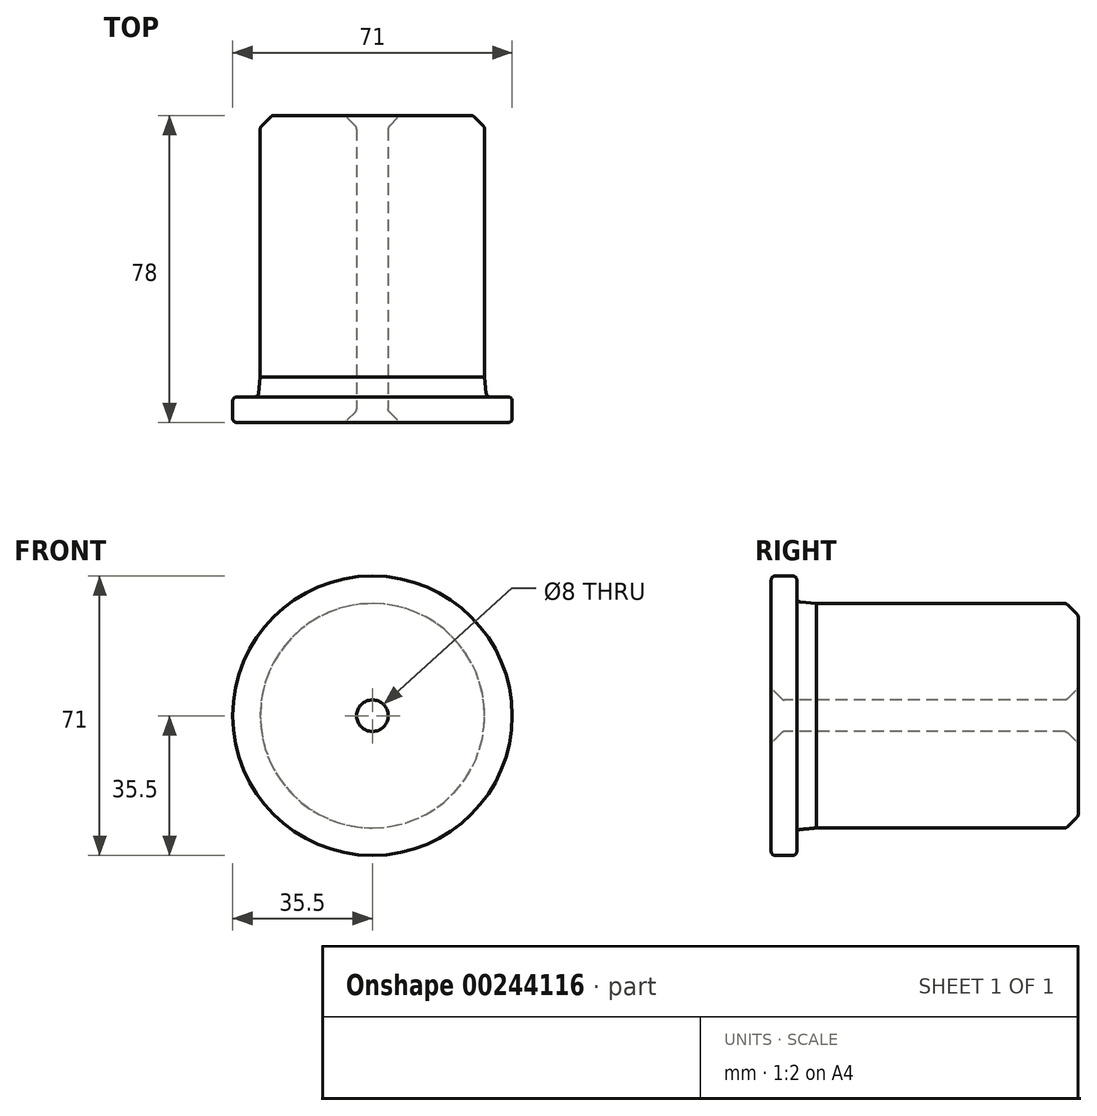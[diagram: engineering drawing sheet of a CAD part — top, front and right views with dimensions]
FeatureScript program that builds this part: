
annotation { "Feature Type Name" : "Feature", "Feature Type Description" : "" }
export const myFeature = defineFeature(function(context is Context, id is Id, definition is map)
    precondition{}
    {
        {
            var Q0;
            Q0=qCreatedBy(makeId("Right.planeOp"),FACE);
            var sketch = newSketch(context, id + "F0", { "sketchPlane" : qUnion([Q0])});
            skLineSegment(sketch, "E0", {"start": v(-14.96, 0) * mm, "end": v(91.12, 0) * mm, "construction": true});
            skLineSegment(sketch, "E1.bottom", {"start": v(0, 4) * mm, "end": v(6.5, 4) * mm});
            skLineSegment(sketch, "E1.top", {"start": v(0, 35.5) * mm, "end": v(6.5, 35.5) * mm});
            skLineSegment(sketch, "E1.left", {"start": v(0, 4) * mm, "end": v(0, 35.5) * mm});
            skLineSegment(sketch, "E1.right", {"start": v(6.5, 4) * mm, "end": v(6.5, 35.5) * mm});
            skLineSegment(sketch, "E2.bottom", {"start": v(78, 4) * mm, "end": v(6.5, 4) * mm});
            skLineSegment(sketch, "E2.top", {"start": v(78, 28.5) * mm, "end": v(6.5, 28.5) * mm});
            skLineSegment(sketch, "E2.left", {"start": v(78, 4) * mm, "end": v(78, 28.5) * mm});
            skLineSegment(sketch, "E2.right", {"start": v(6.5, 4) * mm, "end": v(6.5, 28.5) * mm});
            skSolve(sketch);
        }
        {
            var Q0;
            Q0=makeQuery(id+"F0.imprint","IMPRINT",FACE,{"disambiguationData":[TD([[makeQuery(id+"F0.imprint","IMPRINT",EDGE,{"derivedFrom":sQuery(id+"F0.wireOp",EDGE,"E1.bottom")}),1.0]])]});
            var Q1;
            Q1=makeQuery(id+"F0.imprint","IMPRINT",FACE,{"disambiguationData":[TD([[makeQuery(id+"F0.imprint","IMPRINT",EDGE,{"derivedFrom":sQuery(id+"F0.wireOp",EDGE,"E2.bottom")}),-1.0]])]});
            var Q2;
            Q2=sQuery(id+"F0.wireOp",EDGE,"E0");
            revolve(context, id + "F1", {"entities" : qUnion([Q0, Q1]), "axis" : qUnion([Q2]), "revolveType" : RevolveType.FULL});
        }
        {
            var Q0;
            Q0=makeQuery(id+"F1.opRevolve","SWEPT_EDGE",EDGE,{"disambiguationData":[OSD([sQuery(id+"F0.wireOp",EDGE,"E2.top"),sQuery(id+"F0.wireOp",EDGE,"E2.left")])]});
            var Q1;
            Q1=makeQuery(id+"F1.opRevolve","SWEPT_EDGE",EDGE,{"disambiguationData":[OSD([sQuery(id+"F0.wireOp",EDGE,"E2.bottom"),sQuery(id+"F0.wireOp",EDGE,"E2.left")])]});
            var Q2;
            Q2=makeQuery(id+"F1.opRevolve","SWEPT_EDGE",EDGE,{"disambiguationData":[OSD([sQuery(id+"F0.wireOp",EDGE,"E1.bottom"),sQuery(id+"F0.wireOp",EDGE,"E1.left")])]});
            chamfer(context, id + "F2", {"entities" : qUnion([Q0, Q1, Q2]), "width" : 3 * mm, "tangentPropagation" : true});
        }
        {
            var Q0;
            Q0=makeQuery(id+"F1.opRevolve","SWEPT_EDGE",EDGE,{"disambiguationData":[OSD([sQuery(id+"F0.wireOp",EDGE,"E1.right"),sQuery(id+"F0.wireOp",EDGE,"E2.top"),sQuery(id+"F0.wireOp",EDGE,"E2.right")])]});
            chamfer(context, id + "F3", {"entities" : qUnion([Q0]), "chamferType" : ChamferType.TWO_OFFSETS, "width1" : 5 * mm, "oppositeDirection" : true, "width2" : 0.5 * mm, "tangentPropagation" : true});
        }
        {
            var Q0;
            Q0=makeQuery(id+"F1.opRevolve","SWEPT_EDGE",EDGE,{"disambiguationData":[OSD([sQuery(id+"F0.wireOp",EDGE,"E1.top"),sQuery(id+"F0.wireOp",EDGE,"E1.left")])]});
            var Q1;
            Q1=makeQuery(id+"F1.opRevolve","SWEPT_EDGE",EDGE,{"disambiguationData":[OSD([sQuery(id+"F0.wireOp",EDGE,"E1.top"),sQuery(id+"F0.wireOp",EDGE,"E1.right")])]});
            var Q2;
            {var subQ0=sQuery(id+"F0.wireOp",EDGE,"E1.right");Q2=makeQuery(id+"F3.opChamfer","BLEND_EDGE",EDGE,{"blendedFrom":[makeQuery(id+"F1.opRevolve","SWEPT_EDGE",EDGE,{"disambiguationData":[OSD([subQ0,sQuery(id+"F0.wireOp",EDGE,"E2.top"),sQuery(id+"F0.wireOp",EDGE,"E2.right")])]}),makeQuery(id+"F1.opRevolve","SWEPT_FACE",FACE,{"disambiguationData":[OSD([subQ0])]})],"blendedInto":[makeQuery(id+"F1.opRevolve","SWEPT_FACE",FACE,{"disambiguationData":[OSD([subQ0])]})]});}
            var Q3;
            {var subQ0=sQuery(id+"F0.wireOp",EDGE,"E2.top");Q3=makeQuery(id+"F2.opChamfer","BLEND_EDGE",EDGE,{"blendedFrom":[makeQuery(id+"F1.opRevolve","SWEPT_EDGE",EDGE,{"disambiguationData":[OSD([subQ0,sQuery(id+"F0.wireOp",EDGE,"E2.left")])]}),makeQuery(id+"F1.opRevolve","SWEPT_FACE",FACE,{"disambiguationData":[OSD([subQ0])]})],"blendedInto":[makeQuery(id+"F1.opRevolve","SWEPT_FACE",FACE,{"disambiguationData":[OSD([subQ0])]})]});}
            var Q4;
            {var subQ0=sQuery(id+"F0.wireOp",EDGE,"E2.left");Q4=makeQuery(id+"F2.opChamfer","BLEND_EDGE",EDGE,{"blendedFrom":[makeQuery(id+"F1.opRevolve","SWEPT_EDGE",EDGE,{"disambiguationData":[OSD([sQuery(id+"F0.wireOp",EDGE,"E2.top"),subQ0])]}),makeQuery(id+"F1.opRevolve","SWEPT_FACE",FACE,{"disambiguationData":[OSD([subQ0])]})],"blendedInto":[makeQuery(id+"F1.opRevolve","SWEPT_FACE",FACE,{"disambiguationData":[OSD([subQ0])]})]});}
            var Q5;
            {var subQ0=sQuery(id+"F0.wireOp",EDGE,"E2.bottom");Q5=makeQuery(id+"F2.opChamfer","BLEND_EDGE",EDGE,{"blendedFrom":[makeQuery(id+"F1.opRevolve","SWEPT_EDGE",EDGE,{"disambiguationData":[OSD([subQ0,sQuery(id+"F0.wireOp",EDGE,"E2.left")])]}),makeQuery(id+"F1.opRevolve","SWEPT_FACE",FACE,{"disambiguationData":[OSD([sQuery(id+"F0.wireOp",EDGE,"E1.bottom"),subQ0])]})],"blendedInto":[makeQuery(id+"F1.opRevolve","SWEPT_FACE",FACE,{"disambiguationData":[OSD([sQuery(id+"F0.wireOp",EDGE,"E1.bottom"),subQ0])]})]});}
            var Q6;
            {var subQ0=sQuery(id+"F0.wireOp",EDGE,"E2.left");Q6=makeQuery(id+"F2.opChamfer","BLEND_EDGE",EDGE,{"blendedFrom":[makeQuery(id+"F1.opRevolve","SWEPT_EDGE",EDGE,{"disambiguationData":[OSD([sQuery(id+"F0.wireOp",EDGE,"E2.bottom"),subQ0])]}),makeQuery(id+"F1.opRevolve","SWEPT_FACE",FACE,{"disambiguationData":[OSD([subQ0])]})],"blendedInto":[makeQuery(id+"F1.opRevolve","SWEPT_FACE",FACE,{"disambiguationData":[OSD([subQ0])]})]});}
            var Q7;
            {var subQ0=sQuery(id+"F0.wireOp",EDGE,"E1.left");Q7=makeQuery(id+"F2.opChamfer","BLEND_EDGE",EDGE,{"blendedFrom":[makeQuery(id+"F1.opRevolve","SWEPT_EDGE",EDGE,{"disambiguationData":[OSD([sQuery(id+"F0.wireOp",EDGE,"E1.bottom"),subQ0])]}),makeQuery(id+"F1.opRevolve","SWEPT_FACE",FACE,{"disambiguationData":[OSD([subQ0])]})],"blendedInto":[makeQuery(id+"F1.opRevolve","SWEPT_FACE",FACE,{"disambiguationData":[OSD([subQ0])]})]});}
            var Q8;
            {var subQ0=sQuery(id+"F0.wireOp",EDGE,"E1.bottom");Q8=makeQuery(id+"F2.opChamfer","BLEND_EDGE",EDGE,{"blendedFrom":[makeQuery(id+"F1.opRevolve","SWEPT_EDGE",EDGE,{"disambiguationData":[OSD([subQ0,sQuery(id+"F0.wireOp",EDGE,"E1.left")])]}),makeQuery(id+"F1.opRevolve","SWEPT_FACE",FACE,{"disambiguationData":[OSD([subQ0,sQuery(id+"F0.wireOp",EDGE,"E2.bottom")])]})],"blendedInto":[makeQuery(id+"F1.opRevolve","SWEPT_FACE",FACE,{"disambiguationData":[OSD([subQ0,sQuery(id+"F0.wireOp",EDGE,"E2.bottom")])]})]});}
            fillet(context, id + "F4", {"entities" : qUnion([Q0, Q1, Q2, Q3, Q4, Q5, Q6, Q7, Q8]), "radius" : 1 * mm, "tangentPropagation" : true, "allowEdgeOverflow" : false});
        }
    });
